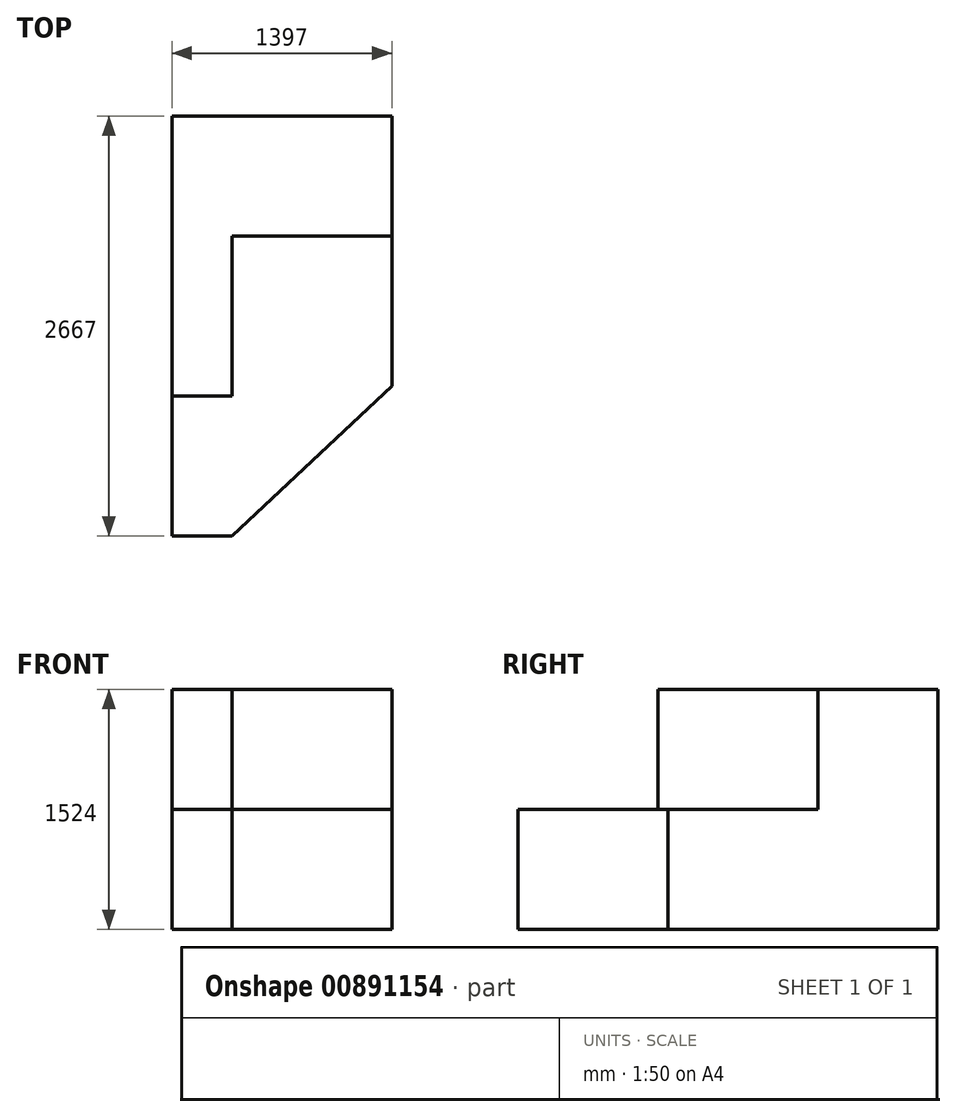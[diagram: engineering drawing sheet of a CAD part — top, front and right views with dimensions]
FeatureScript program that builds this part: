
annotation { "Feature Type Name" : "Feature", "Feature Type Description" : "" }
export const myFeature = defineFeature(function(context is Context, id is Id, definition is map)
    precondition{}
    {
        {
            var Q0;
            Q0=qCreatedBy(makeId("Right.planeOp"),FACE);
            var sketch = newSketch(context, id + "F0", { "sketchPlane" : qUnion([Q0])});
            skLineSegment(sketch, "E0.bottom", {"start": v(0, 0) * mm, "end": v(1778, 0) * mm});
            skLineSegment(sketch, "E0.top", {"start": v(0, -1524) * mm, "end": v(1778, -1524) * mm});
            skLineSegment(sketch, "E0.left", {"start": v(0, 0) * mm, "end": v(0, -1524) * mm});
            skLineSegment(sketch, "E0.right", {"start": v(1778, 0) * mm, "end": v(1778, -1524) * mm});
            skSolve(sketch);
        }
        {
            var Q0;
            Q0=makeQuery(id+"F0.imprint","IMPRINT",FACE,{"disambiguationData":[TD([[makeQuery(id+"F0.imprint","IMPRINT",EDGE,{"derivedFrom":sQuery(id+"F0.wireOp",EDGE,"E0.bottom")}),-1.0]])]});
            var sketch = newSketch(context, id + "F1", { "sketchPlane" : qUnion([Q0])});
            skLineSegment(sketch, "E1.bottom", {"start": v(0, 0) * mm, "end": v(889, 0) * mm});
            skLineSegment(sketch, "E1.top", {"start": v(0, -762) * mm, "end": v(889, -762) * mm});
            skLineSegment(sketch, "E1.left", {"start": v(0, 0) * mm, "end": v(0, -762) * mm});
            skLineSegment(sketch, "E1.right", {"start": v(889, 0) * mm, "end": v(889, -762) * mm});
            skSolve(sketch);
        }
        {
            var Q0;
            Q0=makeQuery(id+"F0.imprint","IMPRINT",FACE,{"disambiguationData":[TD([[makeQuery(id+"F0.imprint","IMPRINT",EDGE,{"derivedFrom":sQuery(id+"F0.wireOp",EDGE,"E0.bottom")}),-1.0]])]});
            extrude(context, id + "F2", {"entities" : qUnion([Q0]), "oppositeDirection" : true, "depth" : 1397 * mm, "offsetDistance" : 25.4 * mm});
        }
        {
            var Q0;
            Q0=makeQuery(id+"F1.imprint","IMPRINT",FACE,{"disambiguationData":[TD([[makeQuery(id+"F1.imprint","IMPRINT",EDGE,{"derivedFrom":sQuery(id+"F1.wireOp",EDGE,"E1.bottom")}),-1.0]])]});
            extrude(context, id + "F3", {"entities" : qUnion([Q0]), "operationType" : NewBodyOperationType.REMOVE, "oppositeDirection" : true, "depth" : 1755.14 * mm, "offsetDistance" : 25.4 * mm});
        }
        {
            var Q0;
            Q0=makeQuery(id+"F2.opExtrude","SWEPT_FACE",FACE,{"disambiguationData":[OSD([sQuery(id+"F0.wireOp",EDGE,"E0.left")])]});
            var sketch = newSketch(context, id + "F4", { "sketchPlane" : qUnion([Q0])});
            skLineSegment(sketch, "E2.bottom", {"start": v(-1397, -762) * mm, "end": v(0, -762) * mm});
            skLineSegment(sketch, "E2.top", {"start": v(-1397, -1524) * mm, "end": v(0, -1524) * mm});
            skLineSegment(sketch, "E2.left", {"start": v(-1397, -762) * mm, "end": v(-1397, -1524) * mm});
            skLineSegment(sketch, "E2.right", {"start": v(0, -762) * mm, "end": v(0, -1524) * mm});
            skSolve(sketch);
        }
        {
            var Q0;
            Q0=makeQuery(id+"F4.imprint","IMPRINT",FACE,{"disambiguationData":[TD([[makeQuery(id+"F4.imprint","IMPRINT",EDGE,{"derivedFrom":sQuery(id+"F4.wireOp",EDGE,"E2.bottom")}),-1.0]])]});
            extrude(context, id + "F5", {"entities" : qUnion([Q0]), "operationType" : NewBodyOperationType.ADD, "depth" : 1016 * mm, "offsetDistance" : 25.4 * mm});
        }
        {
            var Q0;
            Q0=makeQuery(id+"F5.boolean.opBoolean","MERGE",FACE,{"derivedFrom":[makeQuery(id+"F3.boolean.opBoolean","COPY",FACE,{"derivedFrom":makeQuery(id+"F3.opExtrude","SWEPT_FACE",FACE,{"disambiguationData":[OSD([sQuery(id+"F1.wireOp",EDGE,"E1.top")])]})}),makeQuery(id+"F5.opExtrude","SWEPT_FACE",FACE,{"disambiguationData":[OSD([sQuery(id+"F4.wireOp",EDGE,"E2.bottom")])]})]});
            var sketch = newSketch(context, id + "F6", { "sketchPlane" : qUnion([Q0])});
            skLineSegment(sketch, "E3", {"start": v(0, -63.5) * mm, "end": v(-1015.92, -1016) * mm});
            skSolve(sketch);
        }
        {
            var Q0;
            {var subQ0=sQuery(id+"F6.wireOp",EDGE,"E3");Q0=makeQuery(id+"F6.imprint","IMPRINT",FACE,{"disambiguationData":[TD([[makeQuery(id+"F6.imprint","IMPRINT",EDGE,{"derivedFrom":subQ0}),1.0]])]});}
            extrude(context, id + "F7", {"entities" : qUnion([Q0]), "operationType" : NewBodyOperationType.REMOVE, "oppositeDirection" : true, "depth" : 1226.82 * mm, "offsetDistance" : 25.4 * mm});
        }
        {
            var Q0;
            Q0=makeQuery(id+"F3.boolean.opBoolean","COPY",FACE,{"derivedFrom":makeQuery(id+"F3.opExtrude","SWEPT_FACE",FACE,{"disambiguationData":[OSD([sQuery(id+"F1.wireOp",EDGE,"E1.right")])]})});
            var sketch = newSketch(context, id + "F8", { "sketchPlane" : qUnion([Q0])});
            skLineSegment(sketch, "E4.bottom", {"start": v(-1397, -762) * mm, "end": v(-1016, -762) * mm});
            skLineSegment(sketch, "E4.top", {"start": v(-1397, 0) * mm, "end": v(-1016, 0) * mm});
            skLineSegment(sketch, "E4.left", {"start": v(-1397, -762) * mm, "end": v(-1397, 0) * mm});
            skLineSegment(sketch, "E4.right", {"start": v(-1016, -762) * mm, "end": v(-1016, 0) * mm});
            skSolve(sketch);
        }
        {
            var Q0;
            Q0=makeQuery(id+"F8.imprint","IMPRINT",FACE,{"disambiguationData":[TD([[makeQuery(id+"F8.imprint","IMPRINT",EDGE,{"derivedFrom":sQuery(id+"F8.wireOp",EDGE,"E4.bottom")}),1.0]])]});
            extrude(context, id + "F9", {"entities" : qUnion([Q0]), "operationType" : NewBodyOperationType.ADD, "depth" : 1016 * mm, "offsetDistance" : 25.4 * mm});
        }
        {
            var Q0;
            Q0=makeQuery(id+"F9.boolean.opBoolean","MERGE",FACE,{"derivedFrom":[makeQuery(id+"F2.opExtrude","SWEPT_FACE",FACE,{"disambiguationData":[OSD([sQuery(id+"F0.wireOp",EDGE,"E0.bottom")])]}),makeQuery(id+"F9.opExtrude","SWEPT_FACE",FACE,{"disambiguationData":[OSD([sQuery(id+"F8.wireOp",EDGE,"E4.top")])]})]});
            var sketch = newSketch(context, id + "F10", { "sketchPlane" : qUnion([Q0])});
            skLineSegment(sketch, "E5", {"start": v(-1397, 1778) * mm, "end": v(-1397, 1651) * mm});
            skLineSegment(sketch, "E6", {"start": v(-1397, 1651) * mm, "end": v(0, 1651) * mm});
            skLineSegment(sketch, "E7", {"start": v(0, 1778) * mm, "end": v(-1397, 1778) * mm});
            skSolve(sketch);
        }
        {
            var Q0;
            Q0=makeQuery(id+"F10.imprint","IMPRINT",FACE,{"disambiguationData":[TD([[makeQuery(id+"F10.imprint","IMPRINT",EDGE,{"derivedFrom":sQuery(id+"F10.wireOp",EDGE,"E5")}),-1.0]])]});
            extrude(context, id + "F11", {"entities" : qUnion([Q0]), "operationType" : NewBodyOperationType.REMOVE, "oppositeDirection" : true, "depth" : 254000 * mm, "offsetDistance" : 25.4 * mm});
        }
    });
